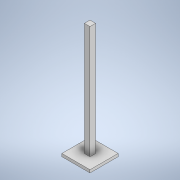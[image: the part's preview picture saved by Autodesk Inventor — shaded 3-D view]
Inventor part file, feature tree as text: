
AUTODESK INVENTOR PART (.ipt)
format: ipt  version: 2020.3 (Build 243373000, 373)  size: 107,520 bytes
history: native  units: mm
features: extrude x2, sketch x2
ambient origin geometry x8: Origin, YZ Plane, XZ Plane, XY Plane, X Axis, Y Axis, Z Axis, Center Point
bodies: Solid1 (feature_tree)
feature tree (4):
  extrude  "Extrusion1"  Depth=50.0mm
  extrude  "Extrusion2"  Depth=20.0mm
  sketch  "Sketch1"  dims[d0=50.0mm d1=50.0mm]
  sketch  "Sketch2"  dims[d2=5.0mm d3=0.0mm d4=20.0mm d5=20.0mm d6=10.0mm d7=10.0mm d8=200.0mm d9=0.0mm]
